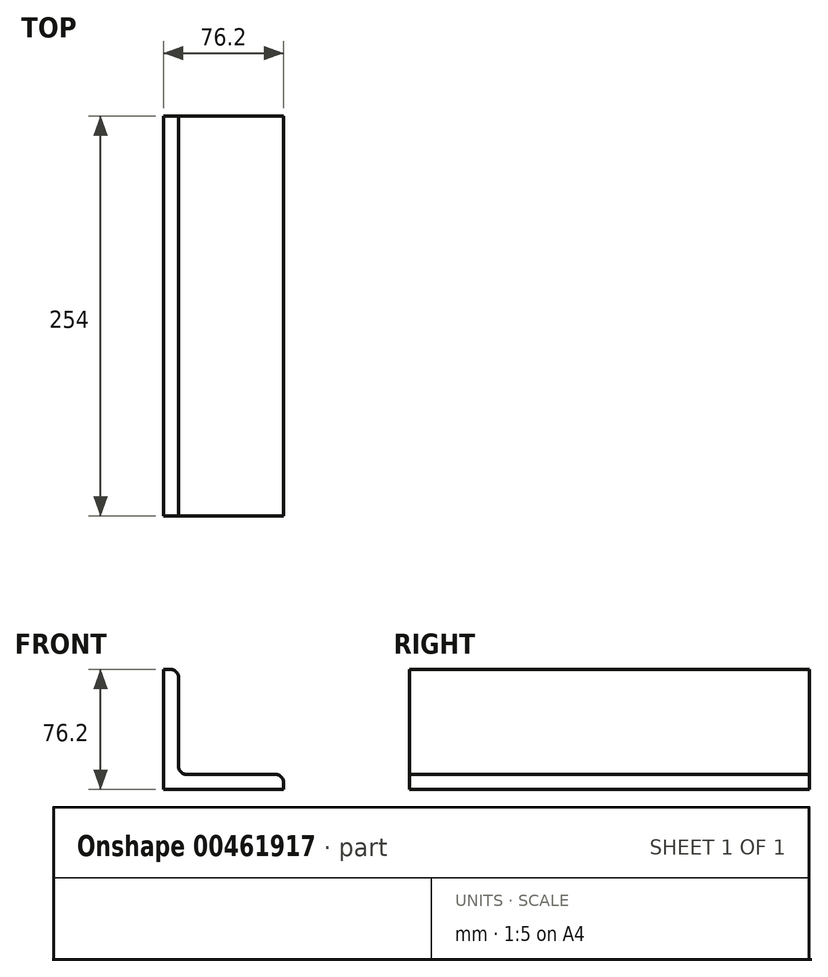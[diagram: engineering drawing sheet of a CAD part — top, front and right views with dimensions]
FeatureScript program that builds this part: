
annotation { "Feature Type Name" : "Feature", "Feature Type Description" : "" }
export const myFeature = defineFeature(function(context is Context, id is Id, definition is map)
    precondition{}
    {
        {
            var Q0;
            Q0=qCreatedBy(makeId("Front.planeOp"),FACE);
            var sketch = newSketch(context, id + "F0", { "sketchPlane" : qUnion([Q0])});
            skLineSegment(sketch, "E0.bottom", {"start": v(38.1, -38.1) * mm, "end": v(-38.1, -38.1) * mm});
            skLineSegment(sketch, "E0.top", {"start": v(-28.57, 38.1) * mm, "end": v(-38.1, 38.1) * mm});
            skLineSegment(sketch, "E0.left", {"start": v(38.1, -38.1) * mm, "end": v(38.1, -28.57) * mm});
            skLineSegment(sketch, "E0.right", {"start": v(-38.1, -38.1) * mm, "end": v(-38.1, 38.1) * mm});
            skPoint(sketch, "E0.middle", {"position": v(0, 0) * mm});
            skLineSegment(sketch, "E1.0", {"start": v(-28.58, -28.58) * mm, "end": v(-28.57, 38.1) * mm});
            skLineSegment(sketch, "E2.0", {"start": v(38.1, -28.57) * mm, "end": v(-28.57, -28.58) * mm});
            skPoint(sketch, "E3.orphan", {"position": v(38.1, 38.1) * mm});
            skSolve(sketch);
        }
        {
            var Q0;
            Q0 = qSketchRegion(id + "F0", true);
            extrude(context, id + "F1", {"entities" : qUnion([Q0]), "endBound" : BoundingType.SYMMETRIC, "depth" : 254 * mm});
        }
        {
            var Q0;
            Q0=makeQuery(id+"F1.opExtrude","SWEPT_EDGE",EDGE,{"disambiguationData":[OSD([sQuery(id+"F0.wireOp",EDGE,"E0.top"),sQuery(id+"F0.wireOp",EDGE,"E1.0")])]});
            var Q1;
            Q1=makeQuery(id+"F1.opExtrude","SWEPT_EDGE",EDGE,{"disambiguationData":[OSD([sQuery(id+"F0.wireOp",EDGE,"E1.0"),sQuery(id+"F0.wireOp",EDGE,"E2.0")])]});
            var Q2;
            Q2=makeQuery(id+"F1.opExtrude","SWEPT_EDGE",EDGE,{"disambiguationData":[OSD([sQuery(id+"F0.wireOp",EDGE,"E0.left"),sQuery(id+"F0.wireOp",EDGE,"E2.0")])]});
            fillet(context, id + "F2", {"entities" : qUnion([Q0, Q1, Q2]), "radius" : 5.08 * mm, "tangentPropagation" : true, "allowEdgeOverflow" : false});
        }
    });
